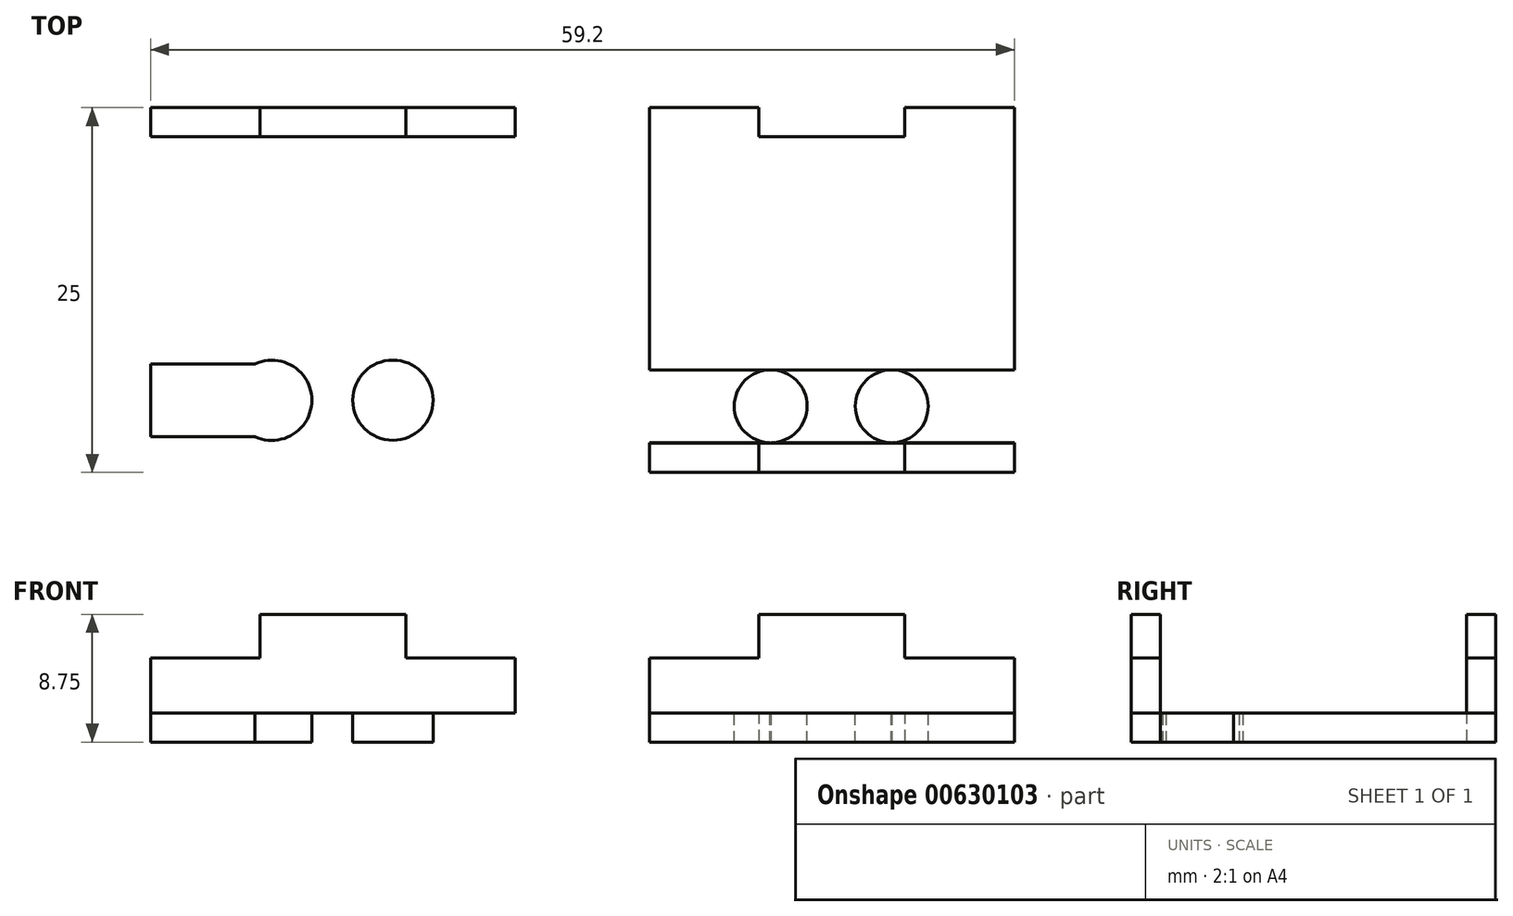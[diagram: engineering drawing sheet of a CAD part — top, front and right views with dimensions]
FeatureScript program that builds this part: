
annotation { "Feature Type Name" : "Feature", "Feature Type Description" : "" }
export const myFeature = defineFeature(function(context is Context, id is Id, definition is map)
    precondition{}
    {
        {
            var Q0;
            Q0=qCreatedBy(makeId("Top.planeOp"),FACE);
            var sketch = newSketch(context, id + "F0", { "sketchPlane" : qUnion([Q0])});
            skLineSegment(sketch, "E0.bottom", {"start": v(12.5, -12.5) * mm, "end": v(-12.5, -12.5) * mm});
            skLineSegment(sketch, "E0.top", {"start": v(12.5, 12.5) * mm, "end": v(-12.5, 12.5) * mm});
            skLineSegment(sketch, "E0.left", {"start": v(12.5, -12.5) * mm, "end": v(12.5, 12.5) * mm});
            skLineSegment(sketch, "E0.right", {"start": v(-12.5, -12.5) * mm, "end": v(-12.5, 12.5) * mm});
            skPoint(sketch, "E0.middle", {"position": v(0, 0) * mm});
            skLineSegment(sketch, "E1", {"start": v(-12.5, 10.5) * mm, "end": v(12.5, 10.5) * mm});
            skLineSegment(sketch, "E2", {"start": v(-12.5, -10.5) * mm, "end": v(12.5, -10.5) * mm});
            skLineSegment(sketch, "E3.bottom", {"start": v(-21.7, -12.5) * mm, "end": v(-46.7, -12.5) * mm});
            skLineSegment(sketch, "E3.top", {"start": v(-21.7, 12.5) * mm, "end": v(-46.7, 12.5) * mm});
            skLineSegment(sketch, "E3.left", {"start": v(-21.7, -12.5) * mm, "end": v(-21.7, 12.5) * mm});
            skLineSegment(sketch, "E3.right", {"start": v(-46.7, -12.5) * mm, "end": v(-46.7, 12.5) * mm});
            skPoint(sketch, "E3.middle", {"position": v(-34.2, 0) * mm});
            skLineSegment(sketch, "E4", {"start": v(-46.7, 10.5) * mm, "end": v(-21.7, 10.5) * mm});
            skLineSegment(sketch, "E5", {"start": v(-46.7, -10.5) * mm, "end": v(-21.7, -10.5) * mm});
            skSolve(sketch);
        }
        {
            var Q0;
            {var subQ0=sQuery(id+"F0.wireOp",EDGE,"E3.top");Q0=makeQuery(id+"F0.imprint","IMPRINT",FACE,{"disambiguationData":[TD([[makeQuery(id+"F0.imprint","IMPRINT",EDGE,{"derivedFrom":subQ0}),1.0]])]});}
            var Q1;
            {var subQ0=sQuery(id+"F0.wireOp",EDGE,"E4");Q1=makeQuery(id+"F0.imprint","IMPRINT",FACE,{"disambiguationData":[TD([[makeQuery(id+"F0.imprint","IMPRINT",EDGE,{"derivedFrom":subQ0}),-1.0]])]});}
            var Q2;
            {var subQ0=sQuery(id+"F0.wireOp",EDGE,"E3.bottom");Q2=makeQuery(id+"F0.imprint","IMPRINT",FACE,{"disambiguationData":[TD([[makeQuery(id+"F0.imprint","IMPRINT",EDGE,{"derivedFrom":subQ0}),-1.0]])]});}
            var Q3;
            {var subQ0=sQuery(id+"F0.wireOp",EDGE,"E0.bottom");Q3=makeQuery(id+"F0.imprint","IMPRINT",FACE,{"disambiguationData":[TD([[makeQuery(id+"F0.imprint","IMPRINT",EDGE,{"derivedFrom":subQ0}),-1.0]])]});}
            var Q4;
            {var subQ0=sQuery(id+"F0.wireOp",EDGE,"E1");Q4=makeQuery(id+"F0.imprint","IMPRINT",FACE,{"disambiguationData":[TD([[makeQuery(id+"F0.imprint","IMPRINT",EDGE,{"derivedFrom":subQ0}),-1.0]])]});}
            var Q5;
            {var subQ0=sQuery(id+"F0.wireOp",EDGE,"E0.top");Q5=makeQuery(id+"F0.imprint","IMPRINT",FACE,{"disambiguationData":[TD([[makeQuery(id+"F0.imprint","IMPRINT",EDGE,{"derivedFrom":subQ0}),1.0]])]});}
            extrude(context, id + "F1", {"entities" : qUnion([Q0, Q1, Q2, Q3, Q4, Q5]), "depth" : 2 * mm, "offsetDistance" : 25 * mm});
        }
        {
            var Q0;
            Q0=makeQuery(id+"F1.opExtrude","CAP_FACE",FACE,{"disambiguationData":[OSD([sQuery(id+"F0.wireOp",EDGE,"E3.bottom"),sQuery(id+"F0.wireOp",EDGE,"E3.top"),sQuery(id+"F0.wireOp",EDGE,"E3.left"),sQuery(id+"F0.wireOp",EDGE,"E3.right")])],"isStart":false});
            var sketch = newSketch(context, id + "F2", { "sketchPlane" : qUnion([Q0])});
            skLineSegment(sketch, "E6.0", {"start": v(-46.7, 10.5) * mm, "end": v(-21.7, 10.5) * mm});
            skLineSegment(sketch, "E6.1", {"start": v(-46.7, -10.5) * mm, "end": v(-21.7, -10.5) * mm});
            skSolve(sketch);
        }
        {
            var Q0;
            Q0=makeQuery(id+"F1.opExtrude","CAP_FACE",FACE,{"disambiguationData":[OSD([sQuery(id+"F0.wireOp",EDGE,"E0.bottom"),sQuery(id+"F0.wireOp",EDGE,"E0.top"),sQuery(id+"F0.wireOp",EDGE,"E0.left"),sQuery(id+"F0.wireOp",EDGE,"E0.right")])],"isStart":false});
            var sketch = newSketch(context, id + "F3", { "sketchPlane" : qUnion([Q0])});
            skLineSegment(sketch, "E7.0", {"start": v(-12.5, 10.5) * mm, "end": v(12.5, 10.5) * mm});
            skLineSegment(sketch, "E7.1", {"start": v(-12.5, -10.5) * mm, "end": v(12.5, -10.5) * mm});
            skSolve(sketch);
        }
        {
            var Q0;
            {var subQ0=sQuery(id+"F2.wireOp",EDGE,"E6.0");Q0=makeQuery(id+"F2.imprint","IMPRINT",FACE,{"disambiguationData":[TD([[makeQuery(id+"F2.imprint","IMPRINT",EDGE,{"derivedFrom":subQ0}),1.0]])]});}
            var Q1;
            {var subQ0=sQuery(id+"F3.wireOp",EDGE,"E7.1");Q1=makeQuery(id+"F3.imprint","IMPRINT",FACE,{"disambiguationData":[TD([[makeQuery(id+"F3.imprint","IMPRINT",EDGE,{"derivedFrom":subQ0}),-1.0]])]});}
            extrude(context, id + "F4", {"entities" : qUnion([Q0, Q1]), "depth" : 3.75 * mm, "offsetDistance" : 25 * mm});
        }
        {
            var Q0;
            Q0=makeQuery(id+"F1.opExtrude","CAP_FACE",FACE,{"disambiguationData":[OSD([sQuery(id+"F0.wireOp",EDGE,"E3.bottom"),sQuery(id+"F0.wireOp",EDGE,"E3.top"),sQuery(id+"F0.wireOp",EDGE,"E3.left"),sQuery(id+"F0.wireOp",EDGE,"E3.right")])],"isStart":false});
            var sketch = newSketch(context, id + "F5", { "sketchPlane" : qUnion([Q0])});
            skLineSegment(sketch, "E8.0", {"start": v(-46.7, -10.5) * mm, "end": v(-21.7, -10.5) * mm});
            skLineSegment(sketch, "E9", {"start": v(-39.2, -12.5) * mm, "end": v(-39.2, -10.5) * mm});
            skLineSegment(sketch, "E10", {"start": v(-29.2, -10.5) * mm, "end": v(-29.2, -12.5) * mm});
            skSolve(sketch);
        }
        {
            var Q0;
            Q0=makeQuery(id+"F1.opExtrude","CAP_FACE",FACE,{"disambiguationData":[OSD([sQuery(id+"F0.wireOp",EDGE,"E0.bottom"),sQuery(id+"F0.wireOp",EDGE,"E0.top"),sQuery(id+"F0.wireOp",EDGE,"E0.left"),sQuery(id+"F0.wireOp",EDGE,"E0.right")])],"isStart":false});
            var sketch = newSketch(context, id + "F6", { "sketchPlane" : qUnion([Q0])});
            skLineSegment(sketch, "E11.0", {"start": v(-12.5, 10.5) * mm, "end": v(12.5, 10.5) * mm});
            skSolve(sketch);
        }
        {
            var Q0;
            {var subQ0=sQuery(id+"F5.wireOp",EDGE,"E9");Q0=makeQuery(id+"F5.imprint","IMPRINT",FACE,{"disambiguationData":[TD([[makeQuery(id+"F5.imprint","IMPRINT",EDGE,{"derivedFrom":subQ0}),-1.0]])]});}
            extrude(context, id + "F7", {"entities" : qUnion([Q0]), "operationType" : NewBodyOperationType.REMOVE, "endBound" : BoundingType.THROUGH_ALL, "oppositeDirection" : true, "depth" : 3.75 * mm, "offsetDistance" : 25 * mm});
        }
        {
            var Q0;
            Q0=makeQuery(id+"F4.opExtrude","CAP_FACE",FACE,{"disambiguationData":[OSD([sQuery(id+"F0.wireOp",EDGE,"E3.top"),sQuery(id+"F0.wireOp",EDGE,"E3.left"),sQuery(id+"F0.wireOp",EDGE,"E3.right"),sQuery(id+"F2.wireOp",EDGE,"E6.0")])],"isStart":false});
            var sketch = newSketch(context, id + "F8", { "sketchPlane" : qUnion([Q0])});
            skPoint(sketch, "E12.endSnap0", {"position": v(-21.7, 11.5) * mm});
            skLineSegment(sketch, "E13", {"start": v(-39.2, 12.5) * mm, "end": v(-39.2, 10.5) * mm});
            skLineSegment(sketch, "E14", {"start": v(-29.2, 12.5) * mm, "end": v(-29.2, 10.5) * mm});
            skSolve(sketch);
        }
        {
            var Q0;
            {var subQ0=sQuery(id+"F8.wireOp",EDGE,"E13");Q0=makeQuery(id+"F8.imprint","IMPRINT",FACE,{"disambiguationData":[TD([[makeQuery(id+"F8.imprint","IMPRINT",EDGE,{"derivedFrom":subQ0}),1.0]])]});}
            extrude(context, id + "F9", {"entities" : qUnion([Q0]), "operationType" : NewBodyOperationType.ADD, "depth" : 3 * mm, "offsetDistance" : 25 * mm});
        }
        {
            var Q0;
            Q0=makeQuery(id+"F4.opExtrude","CAP_FACE",FACE,{"disambiguationData":[OSD([sQuery(id+"F0.wireOp",EDGE,"E0.bottom"),sQuery(id+"F0.wireOp",EDGE,"E0.left"),sQuery(id+"F0.wireOp",EDGE,"E0.right"),sQuery(id+"F3.wireOp",EDGE,"E7.1")])],"isStart":false});
            var sketch = newSketch(context, id + "F10", { "sketchPlane" : qUnion([Q0])});
            skPoint(sketch, "E15.endSnap0", {"position": v(12.5, -11.5) * mm});
            skLineSegment(sketch, "E16", {"start": v(-5, -10.5) * mm, "end": v(-5, -12.5) * mm});
            skPoint(sketch, "E16.endSnap0", {"position": v(0, -12.5) * mm});
            skLineSegment(sketch, "E17", {"start": v(5, -10.5) * mm, "end": v(5, -12.5) * mm});
            skSolve(sketch);
        }
        {
            var Q0;
            {var subQ0=sQuery(id+"F10.wireOp",EDGE,"E16");Q0=makeQuery(id+"F10.imprint","IMPRINT",FACE,{"disambiguationData":[TD([[makeQuery(id+"F10.imprint","IMPRINT",EDGE,{"derivedFrom":subQ0}),1.0]])]});}
            extrude(context, id + "F11", {"entities" : qUnion([Q0]), "operationType" : NewBodyOperationType.ADD, "depth" : 3 * mm, "offsetDistance" : 25 * mm});
        }
        {
            var Q0;
            Q0=makeQuery(id+"F1.opExtrude","SWEPT_FACE",FACE,{"disambiguationData":[OSD([sQuery(id+"F0.wireOp",EDGE,"E0.top")])]});
            var sketch = newSketch(context, id + "F12", { "sketchPlane" : qUnion([Q0])});
            skLineSegment(sketch, "E18", {"start": v(-12.5, 1) * mm, "end": v(0, 1) * mm});
            skLineSegment(sketch, "E19", {"start": v(0, 1) * mm, "end": v(-5, 1) * mm});
            skLineSegment(sketch, "E20", {"start": v(-5, 1) * mm, "end": v(5, 1) * mm});
            skLineSegment(sketch, "E21", {"start": v(-5, 2) * mm, "end": v(-5, 0) * mm});
            skLineSegment(sketch, "E22", {"start": v(5, 2) * mm, "end": v(5, 0) * mm});
            skSolve(sketch);
        }
        {
            var Q0;
            {var subQ1=sQuery(id+"F12.wireOp",EDGE,"E20");var subQ8=makeQuery(id+"F12.imprint","IMPRINT",VERTEX,{"derivedFrom":subQ1});Q0=makeQuery(id+"F12.imprint","IMPRINT",FACE,{"disambiguationData":[TD([[makeQuery(id+"F12.imprint","IMPRINT",EDGE,{"disambiguationData":[TD([[subQ8,-1.0]])],"derivedFrom":subQ1}),1.0]])]});}
            var Q1;
            {var subQ1=sQuery(id+"F12.wireOp",EDGE,"E20");var subQ7=makeQuery(id+"F12.imprint","IMPRINT",VERTEX,{"derivedFrom":subQ1});Q1=makeQuery(id+"F12.imprint","IMPRINT",FACE,{"disambiguationData":[TD([[makeQuery(id+"F12.imprint","IMPRINT",EDGE,{"disambiguationData":[TD([[subQ7,-1.0]])],"derivedFrom":subQ1}),-1.0]])]});}
            extrude(context, id + "F13", {"entities" : qUnion([Q0, Q1]), "operationType" : NewBodyOperationType.REMOVE, "oppositeDirection" : true, "depth" : 2 * mm, "offsetDistance" : 25 * mm});
        }
        {
            var Q0;
            Q0=makeQuery(id+"F1.opExtrude","CAP_FACE",FACE,{"disambiguationData":[OSD([sQuery(id+"F0.wireOp",EDGE,"E0.bottom"),sQuery(id+"F0.wireOp",EDGE,"E0.top"),sQuery(id+"F0.wireOp",EDGE,"E0.left"),sQuery(id+"F0.wireOp",EDGE,"E0.right")])],"isStart":false});
            var sketch = newSketch(context, id + "F14", { "sketchPlane" : qUnion([Q0])});
            skLineSegment(sketch, "E23", {"start": v(12.5, -10.48) * mm, "end": v(-12.5, -10.48) * mm});
            skLineSegment(sketch, "E24", {"start": v(-12.5, -10.48) * mm, "end": v(-12.5, -7.3) * mm});
            skLineSegment(sketch, "E25", {"start": v(12.5, -7.3) * mm, "end": v(12.5, -10.48) * mm});
            skLineSegment(sketch, "E26", {"start": v(-12.5, -5.48) * mm, "end": v(12.5, -5.48) * mm});
            skLineSegment(sketch, "E27", {"start": v(-12.5, -5.48) * mm, "end": v(-12.5, -7.98) * mm});
            skPoint(sketch, "E28", {"position": v(-12.5, -7.98) * mm});
            skPoint(sketch, "E29", {"position": v(-4.2, -7.98) * mm});
            skPoint(sketch, "E30", {"position": v(4.1, -7.98) * mm});
            skCircle(sketch, "E31", {"center": v(-4.2, -7.98) * mm, "radius": 2.5 * mm});
            skCircle(sketch, "E32", {"center": v(4.1, -7.98) * mm, "radius": 2.5 * mm});
            skSolve(sketch);
        }
        {
            var Q0;
            {var subQ0=sQuery(id+"F14.wireOp",EDGE,"E31");var subQ1=sQuery(id+"F14.wireOp",EDGE,"E23");var subQ2=makeQuery(id+"F14.imprint","INTERSECT",VERTEX,{"disambiguationData":[OD(0.0)],"derivedFrom":[subQ1,subQ0]});Q0=makeQuery(id+"F14.imprint","IMPRINT",FACE,{"disambiguationData":[TD([[makeQuery(id+"F14.imprint","IMPRINT",EDGE,{"disambiguationData":[TD([[subQ2,-1.0]])],"derivedFrom":subQ1}),-1.0]])]});}
            var Q1;
            {var subQ0=sQuery(id+"F14.wireOp",EDGE,"E32");var subQ1=sQuery(id+"F14.wireOp",EDGE,"E23");var subQ2=makeQuery(id+"F14.imprint","INTERSECT",VERTEX,{"disambiguationData":[OD(0.0)],"derivedFrom":[subQ1,subQ0]});Q1=makeQuery(id+"F14.imprint","IMPRINT",FACE,{"disambiguationData":[TD([[makeQuery(id+"F14.imprint","IMPRINT",EDGE,{"disambiguationData":[TD([[subQ2,-1.0]])],"derivedFrom":subQ1}),-1.0]])]});}
            extrude(context, id + "F15", {"entities" : qUnion([Q0, Q1]), "operationType" : NewBodyOperationType.REMOVE, "endBound" : BoundingType.THROUGH_ALL, "oppositeDirection" : true, "depth" : 25 * mm, "offsetDistance" : 25 * mm});
        }
        {
            var Q0;
            Q0=makeQuery(id+"F1.opExtrude","CAP_FACE",FACE,{"disambiguationData":[OSD([sQuery(id+"F0.wireOp",EDGE,"E3.bottom"),sQuery(id+"F0.wireOp",EDGE,"E3.top"),sQuery(id+"F0.wireOp",EDGE,"E3.left"),sQuery(id+"F0.wireOp",EDGE,"E3.right")])],"isStart":false});
            var sketch = newSketch(context, id + "F16", { "sketchPlane" : qUnion([Q0])});
            skLineSegment(sketch, "E33", {"start": v(-46.7, -10.06) * mm, "end": v(-21.7, -10.06) * mm});
            skLineSegment(sketch, "E34", {"start": v(-21.7, -10.06) * mm, "end": v(-21.7, -5.06) * mm});
            skLineSegment(sketch, "E35", {"start": v(-21.7, -5.06) * mm, "end": v(-46.7, -5.06) * mm});
            skLineSegment(sketch, "E36", {"start": v(-46.7, -5.06) * mm, "end": v(-46.7, -10.06) * mm});
            skPoint(sketch, "E37", {"position": v(-38.4, -7.56) * mm});
            skPoint(sketch, "E38", {"position": v(-30.1, -7.56) * mm});
            skCircle(sketch, "E39", {"center": v(-38.4, -7.56) * mm, "radius": 2.75 * mm});
            skCircle(sketch, "E40", {"center": v(-30.1, -7.56) * mm, "radius": 2.75 * mm});
            skSolve(sketch);
        }
        {
            var Q0;
            {var subQ0=sQuery(id+"F16.wireOp",EDGE,"SsrMBtT3-KcaX-faK4-uUYD-uQN6NOASxUaH");var subQ1=makeQuery(id+"F16.imprint","INTERSECT",VERTEX,{"derivedFrom":[sQuery(id+"F16.wireOp",EDGE,"nTZc0buc-fOiK-CmYn-821l-0ORg810tBl8e"),subQ0]});Q0=makeQuery(id+"F16.imprint","IMPRINT",FACE,{"disambiguationData":[TD([[makeQuery(id+"F16.imprint","IMPRINT",EDGE,{"disambiguationData":[TD([[subQ1,1.0]])],"derivedFrom":subQ0}),1.0]])]});}
            var Q1;
            {var subQ0=sQuery(id+"F16.wireOp",EDGE,"Hkz7IfqI-PXDv-1dDT-87MU-taTeK0T1yJ76");var subQ1=makeQuery(id+"F16.imprint","INTERSECT",VERTEX,{"derivedFrom":[sQuery(id+"F16.wireOp",EDGE,"nTZc0buc-fOiK-CmYn-821l-0ORg810tBl8e"),subQ0]});Q1=makeQuery(id+"F16.imprint","IMPRINT",FACE,{"disambiguationData":[TD([[makeQuery(id+"F16.imprint","IMPRINT",EDGE,{"disambiguationData":[TD([[subQ1,1.0]])],"derivedFrom":subQ0}),1.0]])]});}
            var Q2;
            {var subQ0=sQuery(id+"F16.wireOp",EDGE,"E39");var subQ1=sQuery(id+"F16.wireOp",EDGE,"E33");var subQ2=makeQuery(id+"F16.imprint","INTERSECT",VERTEX,{"disambiguationData":[OD(0.0)],"derivedFrom":[subQ1,subQ0]});Q2=makeQuery(id+"F16.imprint","IMPRINT",FACE,{"disambiguationData":[TD([[makeQuery(id+"F16.imprint","IMPRINT",EDGE,{"disambiguationData":[TD([[subQ2,-1.0]])],"derivedFrom":subQ1}),1.0]])]});}
            var Q3;
            {var subQ0=sQuery(id+"F16.wireOp",EDGE,"E39");var subQ1=sQuery(id+"F16.wireOp",EDGE,"E35");var subQ2=makeQuery(id+"F16.imprint","INTERSECT",VERTEX,{"disambiguationData":[OD(0.0)],"derivedFrom":[subQ1,subQ0]});Q3=makeQuery(id+"F16.imprint","IMPRINT",FACE,{"disambiguationData":[TD([[makeQuery(id+"F16.imprint","IMPRINT",EDGE,{"disambiguationData":[TD([[subQ2,-1.0]])],"derivedFrom":subQ1}),-1.0]])]});}
            var Q4;
            {var subQ0=sQuery(id+"F16.wireOp",EDGE,"E39");var subQ1=sQuery(id+"F16.wireOp",EDGE,"E33");var subQ2=makeQuery(id+"F16.imprint","INTERSECT",VERTEX,{"disambiguationData":[OD(0.0)],"derivedFrom":[subQ1,subQ0]});Q4=makeQuery(id+"F16.imprint","IMPRINT",FACE,{"disambiguationData":[TD([[makeQuery(id+"F16.imprint","IMPRINT",EDGE,{"disambiguationData":[TD([[subQ2,-1.0]])],"derivedFrom":subQ1}),-1.0]])]});}
            var Q5;
            {var subQ0=sQuery(id+"F16.wireOp",EDGE,"E40");var subQ1=sQuery(id+"F16.wireOp",EDGE,"E33");var subQ2=makeQuery(id+"F16.imprint","INTERSECT",VERTEX,{"disambiguationData":[OD(0.0)],"derivedFrom":[subQ1,subQ0]});Q5=makeQuery(id+"F16.imprint","IMPRINT",FACE,{"disambiguationData":[TD([[makeQuery(id+"F16.imprint","IMPRINT",EDGE,{"disambiguationData":[TD([[subQ2,-1.0]])],"derivedFrom":subQ1}),-1.0]])]});}
            var Q6;
            {var subQ0=sQuery(id+"F16.wireOp",EDGE,"E40");var subQ1=sQuery(id+"F16.wireOp",EDGE,"E33");var subQ2=makeQuery(id+"F16.imprint","INTERSECT",VERTEX,{"disambiguationData":[OD(0.0)],"derivedFrom":[subQ1,subQ0]});Q6=makeQuery(id+"F16.imprint","IMPRINT",FACE,{"disambiguationData":[TD([[makeQuery(id+"F16.imprint","IMPRINT",EDGE,{"disambiguationData":[TD([[subQ2,-1.0]])],"derivedFrom":subQ1}),1.0]])]});}
            var Q7;
            {var subQ0=sQuery(id+"F16.wireOp",EDGE,"E40");var subQ1=sQuery(id+"F16.wireOp",EDGE,"E35");var subQ2=makeQuery(id+"F16.imprint","INTERSECT",VERTEX,{"disambiguationData":[OD(0.0)],"derivedFrom":[subQ1,subQ0]});Q7=makeQuery(id+"F16.imprint","IMPRINT",FACE,{"disambiguationData":[TD([[makeQuery(id+"F16.imprint","IMPRINT",EDGE,{"disambiguationData":[TD([[subQ2,-1.0]])],"derivedFrom":subQ1}),-1.0]])]});}
            extrude(context, id + "F17", {"entities" : qUnion([Q0, Q1, Q2, Q3, Q4, Q5, Q6, Q7]), "operationType" : NewBodyOperationType.REMOVE, "endBound" : BoundingType.THROUGH_ALL, "oppositeDirection" : true, "depth" : 25 * mm, "offsetDistance" : 25 * mm});
        }
    });
